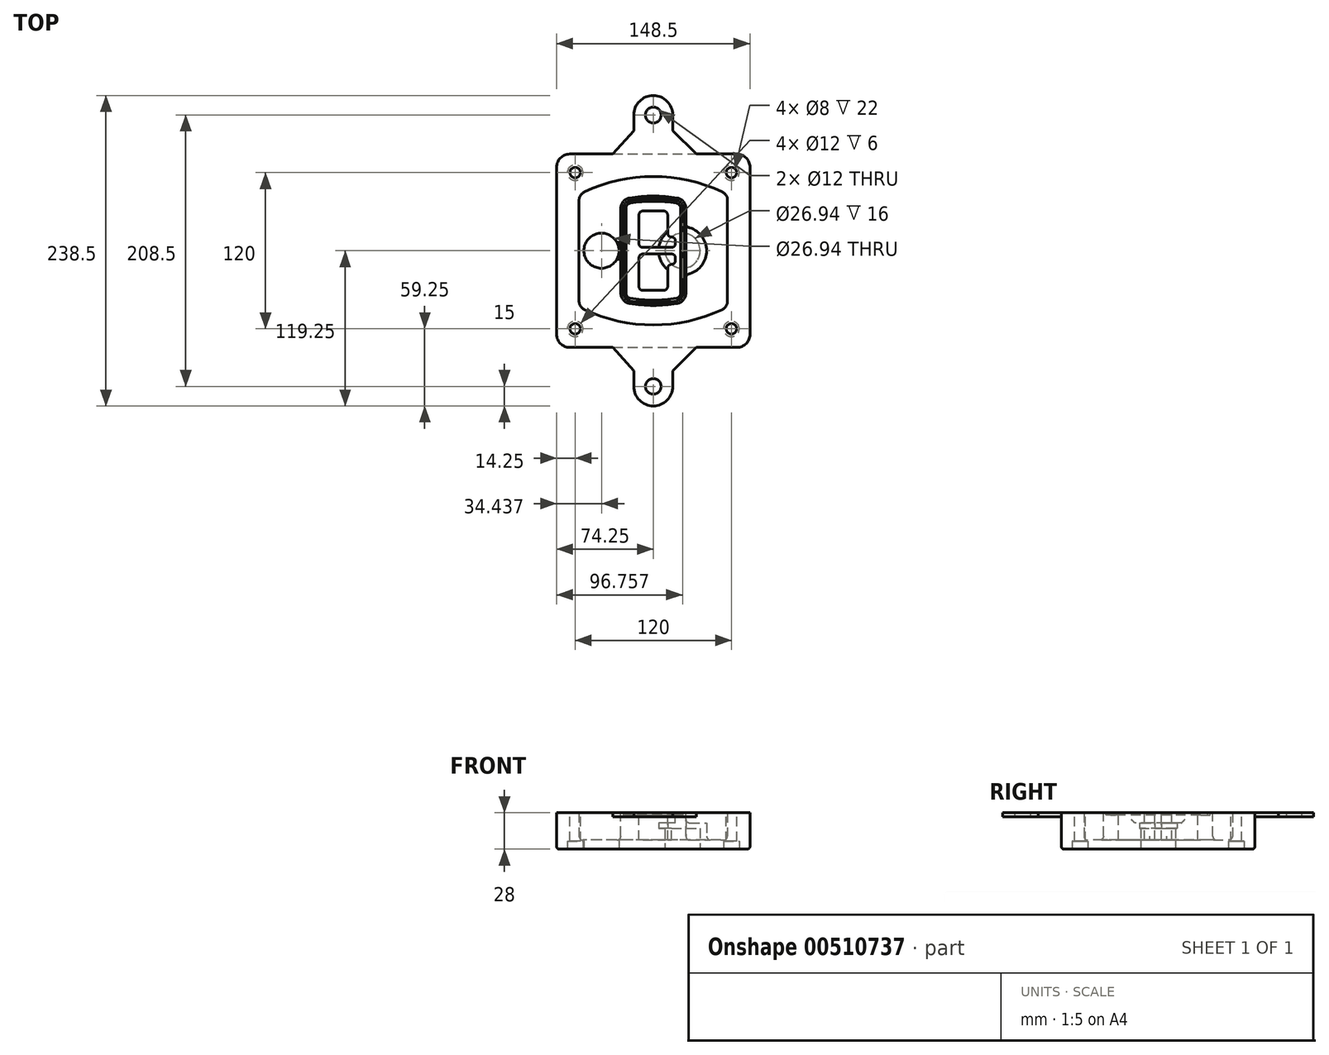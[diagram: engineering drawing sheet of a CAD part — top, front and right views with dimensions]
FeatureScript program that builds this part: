
annotation { "Feature Type Name" : "Feature", "Feature Type Description" : "" }
export const myFeature = defineFeature(function(context is Context, id is Id, definition is map)
    precondition{}
    {
        {
            var Q0;
            Q0=qCreatedBy(makeId("Top.planeOp"),FACE);
            var sketch = newSketch(context, id + "F0", { "sketchPlane" : qUnion([Q0])});
            skPoint(sketch, "E0.rect.middle", {"position": v(0, 0) * mm});
            skLineSegment(sketch, "E1.bottom", {"start": v(-64.25, -74.25) * mm, "end": v(64.25, -74.25) * mm});
            skLineSegment(sketch, "E1.top", {"start": v(-64.25, 74.25) * mm, "end": v(64.25, 74.25) * mm});
            skLineSegment(sketch, "E1.left", {"start": v(-74.25, -64.25) * mm, "end": v(-74.25, 64.25) * mm});
            skLineSegment(sketch, "E1.right", {"start": v(74.25, -64.25) * mm, "end": v(74.25, 64.25) * mm});
            skLineSegment(sketch, "E2", {"start": v(-74.25, 74.25) * mm, "end": v(74.25, -74.25) * mm, "construction": true});
            skLineSegment(sketch, "E3", {"start": v(74.25, 74.25) * mm, "end": v(-74.25, -74.25) * mm, "construction": true});
            skCircle(sketch, "E4", {"center": v(-60, 60) * mm, "radius": 4 * mm});
            skCircle(sketch, "E5", {"center": v(60, 60) * mm, "radius": 4 * mm});
            skCircle(sketch, "E6", {"center": v(60, -60) * mm, "radius": 4 * mm});
            skCircle(sketch, "E7", {"center": v(-60, -60) * mm, "radius": 4 * mm});
            skLineSegment(sketch, "E8", {"start": v(-60, 60) * mm, "end": v(60, 60) * mm, "construction": true});
            skLineSegment(sketch, "E9", {"start": v(60, 60) * mm, "end": v(60, -60) * mm, "construction": true});
            skLineSegment(sketch, "E10", {"start": v(60, -60) * mm, "end": v(-60, -60) * mm, "construction": true});
            skLineSegment(sketch, "E11", {"start": v(-60, -60) * mm, "end": v(-60, 60) * mm, "construction": true});
            skLineSegment(sketch, "E12", {"start": v(-60, 38.83) * mm, "end": v(-60, -38.83) * mm});
            skLineSegment(sketch, "E13", {"start": v(60, 38.83) * mm, "end": v(60, -38.83) * mm});
            skArc(sketch, "E14", {"start": v(54.26, 47.88) * mm, "mid": v(0, 60) * mm, "end": v(-54.26, 47.88) * mm});
            skArc(sketch, "E15", {"start": v(-54.26, -47.88) * mm, "mid": v(0, -60) * mm, "end": v(54.26, -47.88) * mm});
            skLineSegment(sketch, "E16", {"start": v(-60, 0) * mm, "end": v(60, 0) * mm, "construction": true});
            skPoint(sketch, "E17.visualSharp", {"position": v(-60, -45) * mm});
            skArc(sketch, "E17.filletArc", {"start": v(-60, -38.83) * mm, "mid": v(-58.44, -44.2) * mm, "end": v(-54.26, -47.88) * mm});
            skPoint(sketch, "E18.visualSharp", {"position": v(-60, 45) * mm});
            skArc(sketch, "E18.filletArc", {"start": v(-54.26, 47.88) * mm, "mid": v(-58.44, 44.2) * mm, "end": v(-60, 38.83) * mm});
            skPoint(sketch, "E19.visualSharp", {"position": v(60, 45) * mm});
            skArc(sketch, "E19.filletArc", {"start": v(60, 38.83) * mm, "mid": v(58.44, 44.2) * mm, "end": v(54.26, 47.88) * mm});
            skPoint(sketch, "E20.visualSharp", {"position": v(60, -45) * mm});
            skArc(sketch, "E20.filletArc", {"start": v(54.26, -47.88) * mm, "mid": v(58.44, -44.2) * mm, "end": v(60, -38.83) * mm});
            skPoint(sketch, "E21.visualSharp", {"position": v(-74.25, 74.25) * mm});
            skArc(sketch, "E21.filletArc", {"start": v(-64.25, 74.25) * mm, "mid": v(-71.32, 71.32) * mm, "end": v(-74.25, 64.25) * mm});
            skPoint(sketch, "E22.visualSharp", {"position": v(74.25, 74.25) * mm});
            skArc(sketch, "E22.filletArc", {"start": v(74.25, 64.25) * mm, "mid": v(71.32, 71.32) * mm, "end": v(64.25, 74.25) * mm});
            skPoint(sketch, "E23.visualSharp", {"position": v(74.25, -74.25) * mm});
            skArc(sketch, "E23.filletArc", {"start": v(64.25, -74.25) * mm, "mid": v(71.32, -71.32) * mm, "end": v(74.25, -64.25) * mm});
            skPoint(sketch, "E24.visualSharp", {"position": v(-74.25, -74.25) * mm});
            skArc(sketch, "E24.filletArc", {"start": v(-74.25, -64.25) * mm, "mid": v(-71.32, -71.32) * mm, "end": v(-64.25, -74.25) * mm});
            skArc(sketch, "E25.0", {"start": v(57, 38.83) * mm, "mid": v(55.9, 42.58) * mm, "end": v(52.98, 45.17) * mm});
            skLineSegment(sketch, "E25.1", {"start": v(57, 38.83) * mm, "end": v(57, -38.83) * mm});
            skArc(sketch, "E25.2", {"start": v(52.98, -45.17) * mm, "mid": v(55.9, -42.58) * mm, "end": v(57, -38.83) * mm});
            skArc(sketch, "E25.3", {"start": v(-52.98, -45.17) * mm, "mid": v(0, -57) * mm, "end": v(52.98, -45.17) * mm});
            skArc(sketch, "E25.4", {"start": v(-57, -38.83) * mm, "mid": v(-55.9, -42.58) * mm, "end": v(-52.98, -45.17) * mm});
            skArc(sketch, "E25.5", {"start": v(52.98, 45.17) * mm, "mid": v(0, 57) * mm, "end": v(-52.98, 45.17) * mm});
            skLineSegment(sketch, "E25.6", {"start": v(-57, 38.83) * mm, "end": v(-57, -38.83) * mm});
            skArc(sketch, "E25.7", {"start": v(-52.98, 45.17) * mm, "mid": v(-55.9, 42.58) * mm, "end": v(-57, 38.83) * mm});
            skArc(sketch, "E26.0", {"start": v(-55.96, 51.5) * mm, "mid": v(-61.82, 46.33) * mm, "end": v(-64, 38.83) * mm});
            skArc(sketch, "E26.1", {"start": v(55.96, 51.5) * mm, "mid": v(0, 64) * mm, "end": v(-55.96, 51.5) * mm});
            skArc(sketch, "E26.2", {"start": v(64, 38.83) * mm, "mid": v(61.82, 46.33) * mm, "end": v(55.96, 51.5) * mm});
            skLineSegment(sketch, "E26.3", {"start": v(64, 38.83) * mm, "end": v(64, -38.83) * mm});
            skArc(sketch, "E26.4", {"start": v(55.96, -51.5) * mm, "mid": v(61.82, -46.33) * mm, "end": v(64, -38.83) * mm});
            skLineSegment(sketch, "E26.5", {"start": v(-64, 38.83) * mm, "end": v(-64, -38.83) * mm});
            skArc(sketch, "E26.6", {"start": v(-55.96, -51.5) * mm, "mid": v(0, -64) * mm, "end": v(55.96, -51.5) * mm});
            skArc(sketch, "E26.7", {"start": v(-64, -38.83) * mm, "mid": v(-61.82, -46.33) * mm, "end": v(-55.96, -51.5) * mm});
            skSolve(sketch);
        }
        {
            var Q0;
            Q0=makeQuery(id+"F0.imprint","IMPRINT",FACE,{"disambiguationData":[TD([[makeQuery(id+"F0.imprint","IMPRINT",EDGE,{"derivedFrom":sQuery(id+"F0.wireOp",EDGE,"E1.bottom")}),1.0]])]});
            var Q1;
            Q1=makeQuery(id+"F0.imprint","IMPRINT",FACE,{"disambiguationData":[TD([[makeQuery(id+"F0.imprint","IMPRINT",EDGE,{"derivedFrom":sQuery(id+"F0.wireOp",EDGE,"E12")}),1.0]])]});
            var Q2;
            Q2=makeQuery(id+"F0.imprint","IMPRINT",FACE,{"disambiguationData":[TD([[makeQuery(id+"F0.imprint","IMPRINT",EDGE,{"derivedFrom":sQuery(id+"F0.wireOp",EDGE,"E25.0")}),1.0]])]});
            var Q3;
            Q3=makeQuery(id+"F0.imprint","IMPRINT",FACE,{"disambiguationData":[TD([[makeQuery(id+"F0.imprint","IMPRINT",EDGE,{"derivedFrom":sQuery(id+"F0.wireOp",EDGE,"E12")}),-1.0]])]});
            extrude(context, id + "F1", {"entities" : qUnion([Q0, Q1, Q2, Q3]), "oppositeDirection" : true, "depth" : 25 * mm});
        }
        {
            var Q0;
            Q0=makeQuery(id+"F0.imprint","IMPRINT",FACE,{"disambiguationData":[TD([[makeQuery(id+"F0.imprint","IMPRINT",EDGE,{"derivedFrom":sQuery(id+"F0.wireOp",EDGE,"E12")}),1.0]])]});
            extrude(context, id + "F2", {"entities" : qUnion([Q0]), "operationType" : NewBodyOperationType.ADD, "depth" : 3 * mm});
        }
        {
            var Q0;
            Q0=makeQuery(id+"F0.imprint","IMPRINT",FACE,{"disambiguationData":[TD([[makeQuery(id+"F0.imprint","IMPRINT",EDGE,{"derivedFrom":sQuery(id+"F0.wireOp",EDGE,"E25.0")}),1.0]])]});
            extrude(context, id + "F3", {"entities" : qUnion([Q0]), "operationType" : NewBodyOperationType.REMOVE, "oppositeDirection" : true, "depth" : 18 * mm});
        }
        {
            var Q0;
            Q0=makeQuery(id+"F2.opExtrude","CAP_FACE",FACE,{"disambiguationData":[OSD([sQuery(id+"F0.wireOp",EDGE,"E12"),sQuery(id+"F0.wireOp",EDGE,"E13"),sQuery(id+"F0.wireOp",EDGE,"E14"),sQuery(id+"F0.wireOp",EDGE,"E15"),sQuery(id+"F0.wireOp",EDGE,"E17.filletArc"),sQuery(id+"F0.wireOp",EDGE,"E18.filletArc"),sQuery(id+"F0.wireOp",EDGE,"E19.filletArc"),sQuery(id+"F0.wireOp",EDGE,"E20.filletArc"),sQuery(id+"F0.wireOp",EDGE,"E25.0"),sQuery(id+"F0.wireOp",EDGE,"E25.1"),sQuery(id+"F0.wireOp",EDGE,"E25.2"),sQuery(id+"F0.wireOp",EDGE,"E25.3"),sQuery(id+"F0.wireOp",EDGE,"E25.4"),sQuery(id+"F0.wireOp",EDGE,"E25.5"),sQuery(id+"F0.wireOp",EDGE,"E25.6"),sQuery(id+"F0.wireOp",EDGE,"E25.7")])],"isStart":false});
            var sketch = newSketch(context, id + "F4", { "sketchPlane" : qUnion([Q0])});
            skArc(sketch, "E27.0", {"start": v(-18.34, -40.45) * mm, "mid": v(0, -42) * mm, "end": v(18.34, -40.45) * mm});
            skArc(sketch, "E28.0", {"start": v(18.34, 40.45) * mm, "mid": v(0, 42) * mm, "end": v(-18.34, 40.45) * mm});
            skLineSegment(sketch, "E29", {"start": v(-25, 32.57) * mm, "end": v(-25, -32.57) * mm});
            skLineSegment(sketch, "E30", {"start": v(25, 32.57) * mm, "end": v(25, -32.57) * mm});
            skLineSegment(sketch, "E31", {"start": v(-25, 39.1) * mm, "end": v(25, 39.1) * mm, "construction": true});
            skLineSegment(sketch, "E32", {"start": v(-25, -39.1) * mm, "end": v(25, -39.1) * mm, "construction": true});
            skPoint(sketch, "E33.visualSharp", {"position": v(-25, 39.1) * mm});
            skArc(sketch, "E33.filletArc", {"start": v(-18.34, 40.45) * mm, "mid": v(-23.11, 37.73) * mm, "end": v(-25, 32.57) * mm});
            skPoint(sketch, "E34.visualSharp", {"position": v(25, 39.1) * mm});
            skArc(sketch, "E34.filletArc", {"start": v(25, 32.57) * mm, "mid": v(23.11, 37.73) * mm, "end": v(18.34, 40.45) * mm});
            skPoint(sketch, "E35.visualSharp", {"position": v(25, -39.1) * mm});
            skArc(sketch, "E35.filletArc", {"start": v(18.34, -40.45) * mm, "mid": v(23.11, -37.73) * mm, "end": v(25, -32.57) * mm});
            skPoint(sketch, "E36.visualSharp", {"position": v(-25, -39.1) * mm});
            skArc(sketch, "E36.filletArc", {"start": v(-25, -32.57) * mm, "mid": v(-23.11, -37.73) * mm, "end": v(-18.34, -40.45) * mm});
            skArc(sketch, "E37.0", {"start": v(52.98, 45.17) * mm, "mid": v(0, 57) * mm, "end": v(-52.98, 45.17) * mm});
            skArc(sketch, "E37.1", {"start": v(-52.98, 45.17) * mm, "mid": v(-55.9, 42.58) * mm, "end": v(-57, 38.83) * mm});
            skLineSegment(sketch, "E37.2", {"start": v(-57, 38.83) * mm, "end": v(-57, -38.83) * mm});
            skArc(sketch, "E37.3", {"start": v(-57, -38.83) * mm, "mid": v(-55.9, -42.58) * mm, "end": v(-52.98, -45.17) * mm});
            skArc(sketch, "E37.4", {"start": v(-52.98, -45.17) * mm, "mid": v(0, -57) * mm, "end": v(52.98, -45.17) * mm});
            skArc(sketch, "E37.5", {"start": v(52.98, -45.17) * mm, "mid": v(55.9, -42.58) * mm, "end": v(57, -38.83) * mm});
            skLineSegment(sketch, "E37.6", {"start": v(57, 38.83) * mm, "end": v(57, -38.83) * mm});
            skArc(sketch, "E37.7", {"start": v(57, 38.83) * mm, "mid": v(55.9, 42.58) * mm, "end": v(52.98, 45.17) * mm});
            skLineSegment(sketch, "E38.0", {"start": v(23, 32.57) * mm, "end": v(23, -32.57) * mm});
            skArc(sketch, "E38.1", {"start": v(18, -38.48) * mm, "mid": v(21.58, -36.44) * mm, "end": v(23, -32.57) * mm});
            skArc(sketch, "E38.2", {"start": v(-18, -38.48) * mm, "mid": v(0, -40) * mm, "end": v(18, -38.48) * mm});
            skArc(sketch, "E38.3", {"start": v(-23, -32.57) * mm, "mid": v(-21.58, -36.44) * mm, "end": v(-18, -38.48) * mm});
            skLineSegment(sketch, "E38.4", {"start": v(-23, 32.57) * mm, "end": v(-23, -32.57) * mm});
            skArc(sketch, "E38.5", {"start": v(23, 32.57) * mm, "mid": v(21.58, 36.44) * mm, "end": v(18, 38.48) * mm});
            skArc(sketch, "E38.6", {"start": v(-18, 38.48) * mm, "mid": v(-21.58, 36.44) * mm, "end": v(-23, 32.57) * mm});
            skArc(sketch, "E38.7", {"start": v(18, 38.48) * mm, "mid": v(0, 40) * mm, "end": v(-18, 38.48) * mm});
            skArc(sketch, "E39.0", {"start": v(21, 32.57) * mm, "mid": v(20.06, 35.15) * mm, "end": v(17.67, 36.5) * mm});
            skLineSegment(sketch, "E39.1", {"start": v(21, 32.57) * mm, "end": v(21, -32.57) * mm});
            skArc(sketch, "E39.2", {"start": v(17.67, -36.5) * mm, "mid": v(20.06, -35.15) * mm, "end": v(21, -32.57) * mm});
            skArc(sketch, "E39.3", {"start": v(-17.67, -36.5) * mm, "mid": v(0, -38) * mm, "end": v(17.67, -36.5) * mm});
            skArc(sketch, "E39.4", {"start": v(-21, -32.57) * mm, "mid": v(-20.06, -35.15) * mm, "end": v(-17.67, -36.5) * mm});
            skArc(sketch, "E39.5", {"start": v(17.67, 36.5) * mm, "mid": v(0, 38) * mm, "end": v(-17.67, 36.5) * mm});
            skLineSegment(sketch, "E39.6", {"start": v(-21, 32.57) * mm, "end": v(-21, -32.57) * mm});
            skArc(sketch, "E39.7", {"start": v(-17.67, 36.5) * mm, "mid": v(-20.06, 35.15) * mm, "end": v(-21, 32.57) * mm});
            skLineSegment(sketch, "E40", {"start": v(-25, 0) * mm, "end": v(25, 0) * mm, "construction": true});
            skLineSegment(sketch, "E41", {"start": v(-11, 5.5) * mm, "end": v(-11, 27.5) * mm});
            skLineSegment(sketch, "E42", {"start": v(-8, 30.5) * mm, "end": v(8, 30.5) * mm});
            skLineSegment(sketch, "E43", {"start": v(11, 27.5) * mm, "end": v(11, 13.5) * mm});
            skLineSegment(sketch, "E44", {"start": v(14, 10.5) * mm, "end": v(14, 10.5) * mm});
            skLineSegment(sketch, "E45", {"start": v(17, 7.5) * mm, "end": v(17, 5.5) * mm});
            skLineSegment(sketch, "E46", {"start": v(14, 2.5) * mm, "end": v(-8, 2.5) * mm});
            skPoint(sketch, "E47.visualSharp", {"position": v(-11, 30.5) * mm});
            skArc(sketch, "E47.filletArc", {"start": v(-8, 30.5) * mm, "mid": v(-10.12, 29.62) * mm, "end": v(-11, 27.5) * mm});
            skPoint(sketch, "E48.visualSharp", {"position": v(11, 30.5) * mm});
            skArc(sketch, "E48.filletArc", {"start": v(11, 27.5) * mm, "mid": v(10.12, 29.62) * mm, "end": v(8, 30.5) * mm});
            skPoint(sketch, "E49.visualSharp", {"position": v(11, 10.5) * mm});
            skArc(sketch, "E49.filletArc", {"start": v(11, 13.5) * mm, "mid": v(11.88, 11.38) * mm, "end": v(14, 10.5) * mm});
            skPoint(sketch, "E50.visualSharp", {"position": v(17, 10.5) * mm});
            skArc(sketch, "E50.filletArc", {"start": v(17, 7.5) * mm, "mid": v(16.12, 9.62) * mm, "end": v(14, 10.5) * mm});
            skPoint(sketch, "E51.visualSharp", {"position": v(17, 2.5) * mm});
            skArc(sketch, "E51.filletArc", {"start": v(14, 2.5) * mm, "mid": v(16.12, 3.38) * mm, "end": v(17, 5.5) * mm});
            skPoint(sketch, "E52.visualSharp", {"position": v(-11, 2.5) * mm});
            skArc(sketch, "E52.filletArc", {"start": v(-11, 5.5) * mm, "mid": v(-10.12, 3.38) * mm, "end": v(-8, 2.5) * mm});
            skLineSegment(sketch, "E53.0.MirrorCS", {"start": v(14, -2.5) * mm, "end": v(-8, -2.5) * mm});
            skArc(sketch, "E54.0.MirrorCS", {"start": v(-11, -5.5) * mm, "mid": v(-10.12, -3.38) * mm, "end": v(-8, -2.5) * mm});
            skLineSegment(sketch, "E55.0.MirrorCS", {"start": v(-11, -5.5) * mm, "end": v(-11, -27.5) * mm});
            skArc(sketch, "E56.0.MirrorCS", {"start": v(-8, -30.5) * mm, "mid": v(-10.12, -29.62) * mm, "end": v(-11, -27.5) * mm});
            skLineSegment(sketch, "E57.0.MirrorCS", {"start": v(-8, -30.5) * mm, "end": v(8, -30.5) * mm});
            skArc(sketch, "E58.0.MirrorCS", {"start": v(11, -27.5) * mm, "mid": v(10.12, -29.62) * mm, "end": v(8, -30.5) * mm});
            skLineSegment(sketch, "E59.0.MirrorCS", {"start": v(11, -27.5) * mm, "end": v(11, -13.5) * mm});
            skArc(sketch, "E60.0.MirrorCS", {"start": v(11, -13.5) * mm, "mid": v(11.88, -11.38) * mm, "end": v(14, -10.5) * mm});
            skArc(sketch, "E61.0.MirrorCS", {"start": v(17, -7.5) * mm, "mid": v(16.12, -9.62) * mm, "end": v(14, -10.5) * mm});
            skLineSegment(sketch, "E62.0.MirrorCS", {"start": v(17, -7.5) * mm, "end": v(17, -5.5) * mm});
            skArc(sketch, "E63.0.MirrorCS", {"start": v(14, -2.5) * mm, "mid": v(16.12, -3.38) * mm, "end": v(17, -5.5) * mm});
            skSolve(sketch);
        }
        {
            var Q0;
            Q0=makeQuery(id+"F4.imprint","IMPRINT",FACE,{"disambiguationData":[TD([[makeQuery(id+"F4.imprint","IMPRINT",EDGE,{"derivedFrom":sQuery(id+"F4.wireOp",EDGE,"E27.0")}),1.0]])]});
            var Q1;
            Q1=makeQuery(id+"F4.imprint","IMPRINT",FACE,{"disambiguationData":[TD([[makeQuery(id+"F4.imprint","IMPRINT",EDGE,{"derivedFrom":sQuery(id+"F4.wireOp",EDGE,"E38.0")}),-1.0]])]});
            var Q2;
            Q2=makeQuery(id+"F4.imprint","IMPRINT",FACE,{"disambiguationData":[TD([[makeQuery(id+"F4.imprint","IMPRINT",EDGE,{"derivedFrom":sQuery(id+"F4.wireOp",EDGE,"E39.0")}),1.0]])]});
            extrude(context, id + "F5", {"entities" : qUnion([Q0, Q1, Q2]), "operationType" : NewBodyOperationType.ADD, "endBound" : BoundingType.UP_TO_NEXT, "oppositeDirection" : true, "depth" : 25 * mm});
        }
        {
            var Q0;
            Q0=makeQuery(id+"F4.imprint","IMPRINT",FACE,{"disambiguationData":[TD([[makeQuery(id+"F4.imprint","IMPRINT",EDGE,{"derivedFrom":sQuery(id+"F4.wireOp",EDGE,"E38.0")}),-1.0]])]});
            extrude(context, id + "F6", {"entities" : qUnion([Q0]), "operationType" : NewBodyOperationType.REMOVE, "oppositeDirection" : true, "depth" : 2 * mm});
        }
        {
            var Q0;
            Q0=makeQuery(id+"F1.opExtrude","CAP_FACE",FACE,{"disambiguationData":[OSD([sQuery(id+"F0.wireOp",EDGE,"E1.bottom"),sQuery(id+"F0.wireOp",EDGE,"E1.top"),sQuery(id+"F0.wireOp",EDGE,"E1.left"),sQuery(id+"F0.wireOp",EDGE,"E1.right"),sQuery(id+"F0.wireOp",EDGE,"E4"),sQuery(id+"F0.wireOp",EDGE,"E5"),sQuery(id+"F0.wireOp",EDGE,"E6"),sQuery(id+"F0.wireOp",EDGE,"E7"),sQuery(id+"F0.wireOp",EDGE,"E21.filletArc"),sQuery(id+"F0.wireOp",EDGE,"E22.filletArc"),sQuery(id+"F0.wireOp",EDGE,"E23.filletArc"),sQuery(id+"F0.wireOp",EDGE,"E24.filletArc")])],"isStart":false});
            var sketch = newSketch(context, id + "F7", { "sketchPlane" : qUnion([Q0])});
            skCircle(sketch, "E64", {"center": v(22.5, 0) * mm, "radius": 13.47 * mm});
            skCircle(sketch, "E65", {"center": v(-39.81, 0) * mm, "radius": 13.47 * mm});
            skLineSegment(sketch, "E66", {"start": v(74.25, 0) * mm, "end": v(-74.25, 0) * mm});
            skCircle(sketch, "E67", {"center": v(22.5, 0) * mm, "radius": 18.47 * mm});
            skCircle(sketch, "E68", {"center": v(60, -60) * mm, "radius": 6 * mm});
            skCircle(sketch, "E69", {"center": v(-60, -60) * mm, "radius": 6 * mm});
            skCircle(sketch, "E70", {"center": v(-60, 60) * mm, "radius": 6 * mm});
            skCircle(sketch, "E71", {"center": v(60, 60) * mm, "radius": 6 * mm});
            skSolve(sketch);
        }
        {
            var Q0;
            {var subQ1=sQuery(id+"F7.wireOp",EDGE,"E66");var subQ4=sQuery(id+"F7.wireOp",EDGE,"E64");var subQ6=makeQuery(id+"F7.imprint","INTERSECT",VERTEX,{"disambiguationData":[OD(0.0)],"derivedFrom":[subQ4,subQ1]});Q0=makeQuery(id+"F7.imprint","IMPRINT",FACE,{"disambiguationData":[TD([[makeQuery(id+"F7.imprint","IMPRINT",EDGE,{"disambiguationData":[TD([[subQ6,-1.0]])],"derivedFrom":subQ4}),-1.0]])]});}
            var Q1;
            {var subQ0=sQuery(id+"F7.wireOp",EDGE,"E66");var subQ1=sQuery(id+"F7.wireOp",EDGE,"E64");var subQ3=makeQuery(id+"F7.imprint","INTERSECT",VERTEX,{"disambiguationData":[OD(0.0)],"derivedFrom":[subQ1,subQ0]});Q1=makeQuery(id+"F7.imprint","IMPRINT",FACE,{"disambiguationData":[TD([[makeQuery(id+"F7.imprint","IMPRINT",EDGE,{"disambiguationData":[TD([[subQ3,-1.0]])],"derivedFrom":subQ1}),1.0]])]});}
            var Q2;
            {var subQ0=sQuery(id+"F7.wireOp",EDGE,"E66");var subQ1=sQuery(id+"F7.wireOp",EDGE,"E64");var subQ3=makeQuery(id+"F7.imprint","INTERSECT",VERTEX,{"disambiguationData":[OD(0.0)],"derivedFrom":[subQ1,subQ0]});Q2=makeQuery(id+"F7.imprint","IMPRINT",FACE,{"disambiguationData":[TD([[makeQuery(id+"F7.imprint","IMPRINT",EDGE,{"disambiguationData":[TD([[subQ3,1.0]])],"derivedFrom":subQ1}),1.0]])]});}
            var Q3;
            {var subQ1=sQuery(id+"F7.wireOp",EDGE,"E66");var subQ4=sQuery(id+"F7.wireOp",EDGE,"E64");var subQ6=makeQuery(id+"F7.imprint","INTERSECT",VERTEX,{"disambiguationData":[OD(0.0)],"derivedFrom":[subQ4,subQ1]});Q3=makeQuery(id+"F7.imprint","IMPRINT",FACE,{"disambiguationData":[TD([[makeQuery(id+"F7.imprint","IMPRINT",EDGE,{"disambiguationData":[TD([[subQ6,1.0]])],"derivedFrom":subQ4}),-1.0]])]});}
            extrude(context, id + "F8", {"entities" : qUnion([Q0, Q1, Q2, Q3]), "operationType" : NewBodyOperationType.ADD, "oppositeDirection" : true, "depth" : 20 * mm});
        }
        {
            var Q0;
            {var subQ0=sQuery(id+"F7.wireOp",EDGE,"E66");var subQ1=sQuery(id+"F7.wireOp",EDGE,"E64");var subQ3=makeQuery(id+"F7.imprint","INTERSECT",VERTEX,{"disambiguationData":[OD(0.0)],"derivedFrom":[subQ1,subQ0]});Q0=makeQuery(id+"F7.imprint","IMPRINT",FACE,{"disambiguationData":[TD([[makeQuery(id+"F7.imprint","IMPRINT",EDGE,{"disambiguationData":[TD([[subQ3,-1.0]])],"derivedFrom":subQ1}),1.0]])]});}
            var Q1;
            {var subQ0=sQuery(id+"F7.wireOp",EDGE,"E66");var subQ1=sQuery(id+"F7.wireOp",EDGE,"E64");var subQ3=makeQuery(id+"F7.imprint","INTERSECT",VERTEX,{"disambiguationData":[OD(0.0)],"derivedFrom":[subQ1,subQ0]});Q1=makeQuery(id+"F7.imprint","IMPRINT",FACE,{"disambiguationData":[TD([[makeQuery(id+"F7.imprint","IMPRINT",EDGE,{"disambiguationData":[TD([[subQ3,1.0]])],"derivedFrom":subQ1}),1.0]])]});}
            extrude(context, id + "F9", {"entities" : qUnion([Q0, Q1]), "operationType" : NewBodyOperationType.REMOVE, "oppositeDirection" : true, "depth" : 16 * mm});
        }
        {
            var Q0;
            {var subQ0=sQuery(id+"F7.wireOp",EDGE,"E66");var subQ1=sQuery(id+"F7.wireOp",EDGE,"E65");var subQ3=makeQuery(id+"F7.imprint","INTERSECT",VERTEX,{"disambiguationData":[OD(0.0)],"derivedFrom":[subQ1,subQ0]});Q0=makeQuery(id+"F7.imprint","IMPRINT",FACE,{"disambiguationData":[TD([[makeQuery(id+"F7.imprint","IMPRINT",EDGE,{"disambiguationData":[TD([[subQ3,-1.0]])],"derivedFrom":subQ1}),1.0]])]});}
            var Q1;
            {var subQ0=sQuery(id+"F7.wireOp",EDGE,"E66");var subQ1=sQuery(id+"F7.wireOp",EDGE,"E65");var subQ3=makeQuery(id+"F7.imprint","INTERSECT",VERTEX,{"disambiguationData":[OD(0.0)],"derivedFrom":[subQ1,subQ0]});Q1=makeQuery(id+"F7.imprint","IMPRINT",FACE,{"disambiguationData":[TD([[makeQuery(id+"F7.imprint","IMPRINT",EDGE,{"disambiguationData":[TD([[subQ3,1.0]])],"derivedFrom":subQ1}),1.0]])]});}
            extrude(context, id + "F10", {"entities" : qUnion([Q0, Q1]), "operationType" : NewBodyOperationType.REMOVE, "oppositeDirection" : true, "depth" : 25 * mm});
        }
        {
            var Q0;
            Q0=makeQuery(id+"F7.imprint","IMPRINT",FACE,{"disambiguationData":[TD([[makeQuery(id+"F7.imprint","IMPRINT",EDGE,{"derivedFrom":sQuery(id+"F7.wireOp",EDGE,"E68")}),1.0]])]});
            var Q1;
            Q1=makeQuery(id+"F7.imprint","IMPRINT",FACE,{"disambiguationData":[TD([[makeQuery(id+"F7.imprint","IMPRINT",EDGE,{"derivedFrom":makeQuery(id+"F1.opExtrude","CAP_EDGE",EDGE,{"disambiguationData":[OSD([sQuery(id+"F0.wireOp",EDGE,"E5")])],"isStart":false})}),-1.0]])]});
            var Q2;
            Q2=makeQuery(id+"F7.imprint","IMPRINT",FACE,{"disambiguationData":[TD([[makeQuery(id+"F7.imprint","IMPRINT",EDGE,{"derivedFrom":sQuery(id+"F7.wireOp",EDGE,"E69")}),1.0]])]});
            var Q3;
            Q3=makeQuery(id+"F7.imprint","IMPRINT",FACE,{"disambiguationData":[TD([[makeQuery(id+"F7.imprint","IMPRINT",EDGE,{"derivedFrom":makeQuery(id+"F1.opExtrude","CAP_EDGE",EDGE,{"disambiguationData":[OSD([sQuery(id+"F0.wireOp",EDGE,"E4")])],"isStart":false})}),-1.0]])]});
            var Q4;
            Q4=makeQuery(id+"F7.imprint","IMPRINT",FACE,{"disambiguationData":[TD([[makeQuery(id+"F7.imprint","IMPRINT",EDGE,{"derivedFrom":sQuery(id+"F7.wireOp",EDGE,"E70")}),1.0]])]});
            var Q5;
            Q5=makeQuery(id+"F7.imprint","IMPRINT",FACE,{"disambiguationData":[TD([[makeQuery(id+"F7.imprint","IMPRINT",EDGE,{"derivedFrom":makeQuery(id+"F1.opExtrude","CAP_EDGE",EDGE,{"disambiguationData":[OSD([sQuery(id+"F0.wireOp",EDGE,"E7")])],"isStart":false})}),-1.0]])]});
            var Q6;
            Q6=makeQuery(id+"F7.imprint","IMPRINT",FACE,{"disambiguationData":[TD([[makeQuery(id+"F7.imprint","IMPRINT",EDGE,{"derivedFrom":sQuery(id+"F7.wireOp",EDGE,"E71")}),1.0]])]});
            var Q7;
            Q7=makeQuery(id+"F7.imprint","IMPRINT",FACE,{"disambiguationData":[TD([[makeQuery(id+"F7.imprint","IMPRINT",EDGE,{"derivedFrom":makeQuery(id+"F1.opExtrude","CAP_EDGE",EDGE,{"disambiguationData":[OSD([sQuery(id+"F0.wireOp",EDGE,"E6")])],"isStart":false})}),-1.0]])]});
            extrude(context, id + "F11", {"entities" : qUnion([Q0, Q1, Q2, Q3, Q4, Q5, Q6, Q7]), "operationType" : NewBodyOperationType.REMOVE, "oppositeDirection" : true, "depth" : 6 * mm});
        }
        {
            var Q0;
            Q0=makeQuery(id+"F9.boolean.opBoolean","COPY",FACE,{"derivedFrom":makeQuery(id+"F9.opExtrude","CAP_FACE",FACE,{"disambiguationData":[OSD([sQuery(id+"F7.wireOp",EDGE,"E64")])],"isStart":false})});
            var sketch = newSketch(context, id + "F12", { "sketchPlane" : qUnion([Q0])});
            skArc(sketch, "E72.0", {"start": v(11, 14.45) * mm, "mid": v(6.45, 9.13) * mm, "end": v(4.2, 2.5) * mm});
            skArc(sketch, "E72.1", {"start": v(4.2, -2.5) * mm, "mid": v(6.45, -9.13) * mm, "end": v(11, -14.45) * mm});
            skLineSegment(sketch, "E73", {"start": v(4.2, -2.5) * mm, "end": v(14, -2.5) * mm});
            skLineSegment(sketch, "E74.0", {"start": v(14, 2.5) * mm, "end": v(4.2, 2.5) * mm});
            skArc(sketch, "E74.1", {"start": v(14, 2.5) * mm, "mid": v(16.12, 3.38) * mm, "end": v(17, 5.5) * mm});
            skLineSegment(sketch, "E74.2", {"start": v(17, 7.5) * mm, "end": v(17, 5.5) * mm});
            skArc(sketch, "E74.3", {"start": v(17, 7.5) * mm, "mid": v(16.12, 9.62) * mm, "end": v(14, 10.5) * mm});
            skArc(sketch, "E74.4", {"start": v(11, 13.5) * mm, "mid": v(11.88, 11.38) * mm, "end": v(14, 10.5) * mm});
            skLineSegment(sketch, "E74.5", {"start": v(11, 14.45) * mm, "end": v(11, 13.5) * mm});
            skLineSegment(sketch, "E74.7", {"start": v(14, -2.5) * mm, "end": v(4.2, -2.5) * mm});
            skArc(sketch, "E74.8", {"start": v(14, -2.5) * mm, "mid": v(16.12, -3.38) * mm, "end": v(17, -5.5) * mm});
            skLineSegment(sketch, "E74.9", {"start": v(17, -7.5) * mm, "end": v(17, -5.5) * mm});
            skArc(sketch, "E74.10", {"start": v(17, -7.5) * mm, "mid": v(16.12, -9.62) * mm, "end": v(14, -10.5) * mm});
            skArc(sketch, "E74.11", {"start": v(11, -13.5) * mm, "mid": v(11.88, -11.38) * mm, "end": v(14, -10.5) * mm});
            skLineSegment(sketch, "E74.12", {"start": v(11, -14.45) * mm, "end": v(11, -13.5) * mm});
            skPoint(sketch, "E75.orphan", {"position": v(11, -27.5) * mm});
            skPoint(sketch, "E76.orphan", {"position": v(-8, -2.5) * mm});
            skPoint(sketch, "E77.orphan", {"position": v(-8, 2.5) * mm});
            skPoint(sketch, "E78.orphan", {"position": v(11, 27.5) * mm});
            skSolve(sketch);
        }
        {
            var Q0;
            {var subQ7=sQuery(id+"F12.wireOp",EDGE,"E72.0");var subQ14=sQuery(id+"F12.wireOp",EDGE,"E72.1");var subQ16=sQuery(id+"F12.wireOp",EDGE,"E74.1");var subQ18=sQuery(id+"F12.wireOp",EDGE,"E74.8");Q0=qUnion([makeQuery(id+"F12.imprint","IMPRINT",FACE,{"disambiguationData":[TD([[makeQuery(id+"F12.imprint","IMPRINT",EDGE,{"derivedFrom":subQ7}),1.0]])]}),makeQuery(id+"F12.imprint","IMPRINT",FACE,{"disambiguationData":[TD([[makeQuery(id+"F12.imprint","IMPRINT",EDGE,{"derivedFrom":subQ14}),1.0]])]}),makeQuery(id+"F12.imprint","IMPRINT",FACE,{"disambiguationData":[TD([[makeQuery(id+"F12.imprint","IMPRINT",EDGE,{"derivedFrom":subQ16}),1.0]])]}),makeQuery(id+"F12.imprint","IMPRINT",FACE,{"disambiguationData":[TD([[makeQuery(id+"F12.imprint","IMPRINT",EDGE,{"derivedFrom":subQ18}),-1.0]])]})]);}
            var Q1;
            Q1=makeQuery(id+"F5.boolean.opBoolean","SPLIT",FACE,{"disambiguationData":[TD([makeQuery(id+"F5.opExtrude","SWEPT_FACE",FACE,{"disambiguationData":[OSD([sQuery(id+"F4.wireOp",EDGE,"E41")])]})])],"derivedFrom":makeQuery(id+"F3.boolean.opBoolean","COPY",FACE,{"derivedFrom":makeQuery(id+"F3.opExtrude","CAP_FACE",FACE,{"disambiguationData":[OSD([sQuery(id+"F0.wireOp",EDGE,"E25.0"),sQuery(id+"F0.wireOp",EDGE,"E25.1"),sQuery(id+"F0.wireOp",EDGE,"E25.2"),sQuery(id+"F0.wireOp",EDGE,"E25.3"),sQuery(id+"F0.wireOp",EDGE,"E25.4"),sQuery(id+"F0.wireOp",EDGE,"E25.5"),sQuery(id+"F0.wireOp",EDGE,"E25.6"),sQuery(id+"F0.wireOp",EDGE,"E25.7")])],"isStart":false})})});
            extrude(context, id + "F13", {"entities" : qUnion([Q0]), "operationType" : NewBodyOperationType.REMOVE, "endBound" : BoundingType.UP_TO_SURFACE, "endBoundEntityFace" : qUnion([Q1]), "depth" : 25 * mm});
        }
        {
            var Q0;
            Q0=makeQuery(id+"F3.boolean.opBoolean","COPY",EDGE,{"derivedFrom":makeQuery(id+"F3.opExtrude","CAP_EDGE",EDGE,{"disambiguationData":[OSD([sQuery(id+"F0.wireOp",EDGE,"E25.6")])],"isStart":false})});
            var Q1;
            Q1=makeQuery(id+"F8.boolean.opBoolean","INTERSECT",EDGE,{"derivedFrom":[makeQuery(id+"F5.opExtrude","SWEPT_FACE",FACE,{"disambiguationData":[OSD([sQuery(id+"F4.wireOp",EDGE,"E30")])]}),makeQuery(id+"F8.opExtrude","CAP_FACE",FACE,{"disambiguationData":[OSD([sQuery(id+"F7.wireOp",EDGE,"E67")])],"isStart":false})]});
            var Q2;
            Q2=makeQuery(id+"F8.boolean.opBoolean","INTERSECT",EDGE,{"disambiguationData":[OD(1.0)],"derivedFrom":[makeQuery(id+"F5.opExtrude","SWEPT_FACE",FACE,{"disambiguationData":[OSD([sQuery(id+"F4.wireOp",EDGE,"E30")])]}),makeQuery(id+"F8.opExtrude","SWEPT_FACE",FACE,{"disambiguationData":[OSD([sQuery(id+"F7.wireOp",EDGE,"E67")])]})]});
            var Q3;
            {var subQ0=sQuery(id+"F4.wireOp",EDGE,"E30");Q3=makeQuery(id+"F8.boolean.opBoolean","SPLIT",EDGE,{"disambiguationData":[TD([makeQuery(id+"F5.opExtrude","SWEPT_FACE",FACE,{"disambiguationData":[OSD([sQuery(id+"F4.wireOp",EDGE,"E35.filletArc")])]})])],"derivedFrom":makeQuery(id+"F5.opExtrude","CAP_EDGE",EDGE,{"disambiguationData":[OSD([subQ0])],"isStart":false})});}
            var Q4;
            {var subQ0=sQuery(id+"F0.wireOp",EDGE,"E25.7");var subQ1=sQuery(id+"F0.wireOp",EDGE,"E25.1");var subQ2=sQuery(id+"F0.wireOp",EDGE,"E25.6");var subQ3=sQuery(id+"F0.wireOp",EDGE,"E25.5");var subQ4=sQuery(id+"F0.wireOp",EDGE,"E25.4");var subQ5=sQuery(id+"F0.wireOp",EDGE,"E25.0");var subQ6=sQuery(id+"F0.wireOp",EDGE,"E25.2");var subQ7=sQuery(id+"F0.wireOp",EDGE,"E25.3");Q4=makeQuery(id+"F8.boolean.opBoolean","INTERSECT",EDGE,{"derivedFrom":[makeQuery(id+"F5.boolean.opBoolean","SPLIT",FACE,{"disambiguationData":[TD([makeQuery(id+"F2.opExtrude","SWEPT_FACE",FACE,{"disambiguationData":[OSD([subQ5])]})])],"derivedFrom":makeQuery(id+"F3.boolean.opBoolean","COPY",FACE,{"derivedFrom":makeQuery(id+"F3.opExtrude","CAP_FACE",FACE,{"disambiguationData":[OSD([subQ5,subQ1,subQ6,subQ7,subQ4,subQ3,subQ2,subQ0])],"isStart":false})})}),makeQuery(id+"F8.opExtrude","SWEPT_FACE",FACE,{"disambiguationData":[OSD([sQuery(id+"F7.wireOp",EDGE,"E67")])]})]});}
            var Q5;
            Q5=makeQuery(id+"F8.boolean.opBoolean","INTERSECT",EDGE,{"disambiguationData":[OD(0.0)],"derivedFrom":[makeQuery(id+"F5.opExtrude","SWEPT_FACE",FACE,{"disambiguationData":[OSD([sQuery(id+"F4.wireOp",EDGE,"E30")])]}),makeQuery(id+"F8.opExtrude","SWEPT_FACE",FACE,{"disambiguationData":[OSD([sQuery(id+"F7.wireOp",EDGE,"E67")])]})]});
            fillet(context, id + "F14", {"entities" : qUnion([Q0, Q1, Q2, Q3, Q4, Q5]), "radius" : 3 * mm, "tangentPropagation" : true, "allowEdgeOverflow" : false});
        }
        {
            var Q0;
            Q0=makeQuery(id+"F1.opExtrude","CAP_EDGE",EDGE,{"disambiguationData":[OSD([sQuery(id+"F0.wireOp",EDGE,"E1.bottom")])],"isStart":false});
            fillet(context, id + "F15", {"entities" : qUnion([Q0]), "radius" : 2 * mm, "tangentPropagation" : true, "allowEdgeOverflow" : false});
        }
        {
            var Q0;
            {var subQ0=sQuery(id+"F0.wireOp",EDGE,"E21.filletArc");var subQ1=sQuery(id+"F0.wireOp",EDGE,"E7");var subQ2=sQuery(id+"F0.wireOp",EDGE,"E6");var subQ3=sQuery(id+"F0.wireOp",EDGE,"E5");var subQ4=sQuery(id+"F0.wireOp",EDGE,"E4");var subQ5=sQuery(id+"F0.wireOp",EDGE,"E22.filletArc");var subQ6=sQuery(id+"F0.wireOp",EDGE,"E1.bottom");var subQ7=sQuery(id+"F0.wireOp",EDGE,"E1.right");var subQ8=sQuery(id+"F0.wireOp",EDGE,"E1.top");var subQ9=sQuery(id+"F0.wireOp",EDGE,"E1.left");var subQ10=sQuery(id+"F0.wireOp",EDGE,"E23.filletArc");var subQ11=sQuery(id+"F0.wireOp",EDGE,"E24.filletArc");Q0=makeQuery(id+"F2.boolean.opBoolean","SPLIT",FACE,{"disambiguationData":[TD([makeQuery(id+"F1.opExtrude","SWEPT_FACE",FACE,{"disambiguationData":[OSD([subQ6])]})])],"derivedFrom":makeQuery(id+"F1.opExtrude","CAP_FACE",FACE,{"disambiguationData":[OSD([subQ6,subQ8,subQ9,subQ7,subQ4,subQ3,subQ2,subQ1,subQ0,subQ5,subQ10,subQ11])],"isStart":true})});}
            var sketch = newSketch(context, id + "F16", { "sketchPlane" : qUnion([Q0])});
            skLineSegment(sketch, "E79", {"start": v(0, 74.25) * mm, "end": v(0, 104.25) * mm, "construction": true});
            skLineSegment(sketch, "E80", {"start": v(-31.1, 74.25) * mm, "end": v(-15, 92.25) * mm});
            skLineSegment(sketch, "E81", {"start": v(-15, 92.25) * mm, "end": v(-15, 104.25) * mm});
            skLineSegment(sketch, "E82", {"start": v(33, 74.25) * mm, "end": v(15, 92.25) * mm});
            skLineSegment(sketch, "E83", {"start": v(15, 92.25) * mm, "end": v(15, 104.25) * mm});
            skArc(sketch, "E84", {"start": v(15, 104.25) * mm, "mid": v(0, 119.25) * mm, "end": v(-15, 104.25) * mm});
            skCircle(sketch, "E85", {"center": v(0, 104.25) * mm, "radius": 6 * mm});
            skLineSegment(sketch, "E86", {"start": v(-74.25, 0) * mm, "end": v(74.25, 0) * mm, "construction": true});
            skLineSegment(sketch, "E87.MirrorCS", {"start": v(0, -74.25) * mm, "end": v(0, -104.25) * mm, "construction": true});
            skLineSegment(sketch, "E88.MirrorCS", {"start": v(-31.1, -74.25) * mm, "end": v(-15, -92.25) * mm});
            skLineSegment(sketch, "E89.MirrorCS", {"start": v(-15, -92.25) * mm, "end": v(-15, -104.25) * mm});
            skArc(sketch, "E90.MirrorCS", {"start": v(15, -104.25) * mm, "mid": v(0, -119.25) * mm, "end": v(-15, -104.25) * mm});
            skCircle(sketch, "E91.MirrorC", {"center": v(0, -104.25) * mm, "radius": 6 * mm});
            skLineSegment(sketch, "E92.MirrorCS", {"start": v(15, -92.25) * mm, "end": v(15, -104.25) * mm});
            skLineSegment(sketch, "E93.MirrorCS", {"start": v(33, -74.25) * mm, "end": v(15, -92.25) * mm});
            skSolve(sketch);
        }
        {
            var Q0;
            {var subQ1=sQuery(id+"F16.wireOp",EDGE,"E80");Q0=makeQuery(id+"F16.imprint","IMPRINT",FACE,{"disambiguationData":[TD([[makeQuery(id+"F16.imprint","IMPRINT",EDGE,{"derivedFrom":subQ1}),-1.0]])]});}
            var Q1;
            Q1=makeQuery(id+"F16.imprint","IMPRINT",FACE,{"disambiguationData":[TD([[makeQuery(id+"F16.imprint","IMPRINT",EDGE,{"derivedFrom":makeQuery(id+"F1.opExtrude","CAP_EDGE",EDGE,{"disambiguationData":[OSD([sQuery(id+"F0.wireOp",EDGE,"E1.left")])],"isStart":true})}),-1.0]])]});
            var Q2;
            {var subQ0=sQuery(id+"F16.wireOp",EDGE,"E88.MirrorCS");Q2=makeQuery(id+"F16.imprint","IMPRINT",FACE,{"disambiguationData":[TD([[makeQuery(id+"F16.imprint","IMPRINT",EDGE,{"derivedFrom":subQ0}),1.0]])]});}
            var Q3;
            {var subQ0=sQuery(id+"F4.wireOp",EDGE,"E36.filletArc");var subQ1=sQuery(id+"F4.wireOp",EDGE,"E35.filletArc");var subQ2=sQuery(id+"F4.wireOp",EDGE,"E34.filletArc");var subQ3=sQuery(id+"F4.wireOp",EDGE,"E33.filletArc");var subQ4=sQuery(id+"F4.wireOp",EDGE,"E27.0");var subQ5=sQuery(id+"F4.wireOp",EDGE,"E30");var subQ6=sQuery(id+"F4.wireOp",EDGE,"E28.0");var subQ7=sQuery(id+"F4.wireOp",EDGE,"E29");Q3=makeQuery(id+"F6.boolean.opBoolean","SPLIT",FACE,{"disambiguationData":[TD([makeQuery(id+"F5.opExtrude","SWEPT_FACE",FACE,{"disambiguationData":[OSD([subQ4])]})])],"derivedFrom":makeQuery(id+"F5.opExtrude","CAP_FACE",FACE,{"disambiguationData":[OSD([subQ4,subQ6,subQ7,subQ5,subQ3,subQ2,subQ1,subQ0,sQuery(id+"F4.wireOp",EDGE,"E41"),sQuery(id+"F4.wireOp",EDGE,"E42"),sQuery(id+"F4.wireOp",EDGE,"E43"),sQuery(id+"F4.wireOp",EDGE,"E45"),sQuery(id+"F4.wireOp",EDGE,"E46"),sQuery(id+"F4.wireOp",EDGE,"E47.filletArc"),sQuery(id+"F4.wireOp",EDGE,"E48.filletArc"),sQuery(id+"F4.wireOp",EDGE,"E49.filletArc"),sQuery(id+"F4.wireOp",EDGE,"E50.filletArc"),sQuery(id+"F4.wireOp",EDGE,"E51.filletArc"),sQuery(id+"F4.wireOp",EDGE,"E52.filletArc"),sQuery(id+"F4.wireOp",EDGE,"E53.0.MirrorCS"),sQuery(id+"F4.wireOp",EDGE,"E54.0.MirrorCS"),sQuery(id+"F4.wireOp",EDGE,"E55.0.MirrorCS"),sQuery(id+"F4.wireOp",EDGE,"E56.0.MirrorCS"),sQuery(id+"F4.wireOp",EDGE,"E57.0.MirrorCS"),sQuery(id+"F4.wireOp",EDGE,"E58.0.MirrorCS"),sQuery(id+"F4.wireOp",EDGE,"E59.0.MirrorCS"),sQuery(id+"F4.wireOp",EDGE,"E60.0.MirrorCS"),sQuery(id+"F4.wireOp",EDGE,"E61.0.MirrorCS"),sQuery(id+"F4.wireOp",EDGE,"E62.0.MirrorCS"),sQuery(id+"F4.wireOp",EDGE,"E63.0.MirrorCS")])],"isStart":true})});}
            extrude(context, id + "F17", {"entities" : qUnion([Q0, Q1, Q2]), "operationType" : NewBodyOperationType.ADD, "endBound" : BoundingType.UP_TO_SURFACE, "endBoundEntityFace" : qUnion([Q3]), "depth" : 25 * mm});
        }
    });
